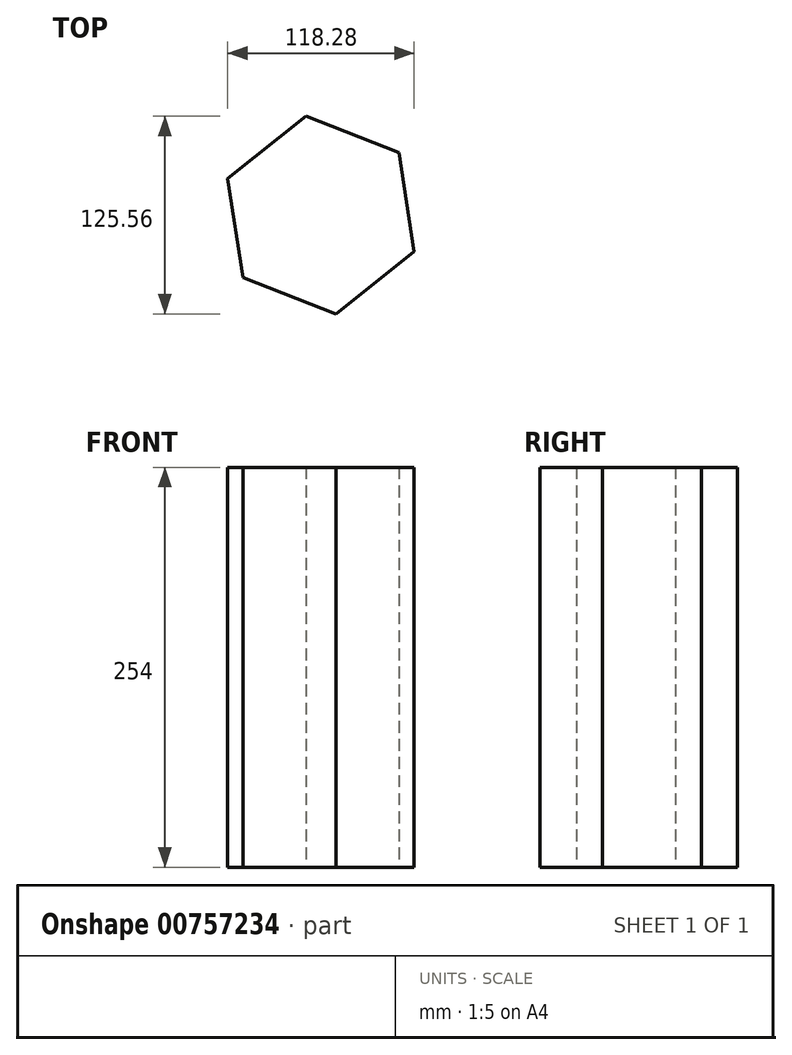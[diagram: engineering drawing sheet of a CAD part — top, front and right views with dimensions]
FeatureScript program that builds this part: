
annotation { "Feature Type Name" : "Feature", "Feature Type Description" : "" }
export const myFeature = defineFeature(function(context is Context, id is Id, definition is map)
    precondition{}
    {
        {
            var Q0;
            Q0=qCreatedBy(makeId("Top.planeOp"),FACE);
            var sketch = newSketch(context, id + "F0", { "sketchPlane" : qUnion([Q0])});
            skCircle(sketch, "E0.cCircle", {"center": v(0, 0) * mm, "radius": 55 * mm, "construction": true});
            skLineSegment(sketch, "E0.0", {"start": v(49.6, 39.65) * mm, "end": v(59.14, -23.13) * mm});
            skLineSegment(sketch, "E0.1", {"start": v(59.14, -23.13) * mm, "end": v(9.54, -62.78) * mm});
            skLineSegment(sketch, "E0.2", {"start": v(9.54, -62.78) * mm, "end": v(-49.6, -39.65) * mm});
            skLineSegment(sketch, "E0.3", {"start": v(-49.6, -39.65) * mm, "end": v(-59.14, 23.13) * mm});
            skLineSegment(sketch, "E0.4", {"start": v(-59.14, 23.13) * mm, "end": v(-9.54, 62.78) * mm});
            skLineSegment(sketch, "E0.5", {"start": v(-9.54, 62.78) * mm, "end": v(49.6, 39.65) * mm});
            skPoint(sketch, "E0.0.midPoint", {"position": v(54.37, 8.26) * mm});
            skSolve(sketch);
        }
        {
            var Q0;
            Q0=makeQuery(id+"F0.imprint","IMPRINT",FACE,{"disambiguationData":[TD([[makeQuery(id+"F0.imprint","IMPRINT",EDGE,{"derivedFrom":sQuery(id+"F0.wireOp",EDGE,"E0.0")}),-1.0]])]});
            extrude(context, id + "F1", {"entities" : qUnion([Q0]), "depth" : 254 * mm, "offsetDistance" : 25.4 * mm});
        }
    });
